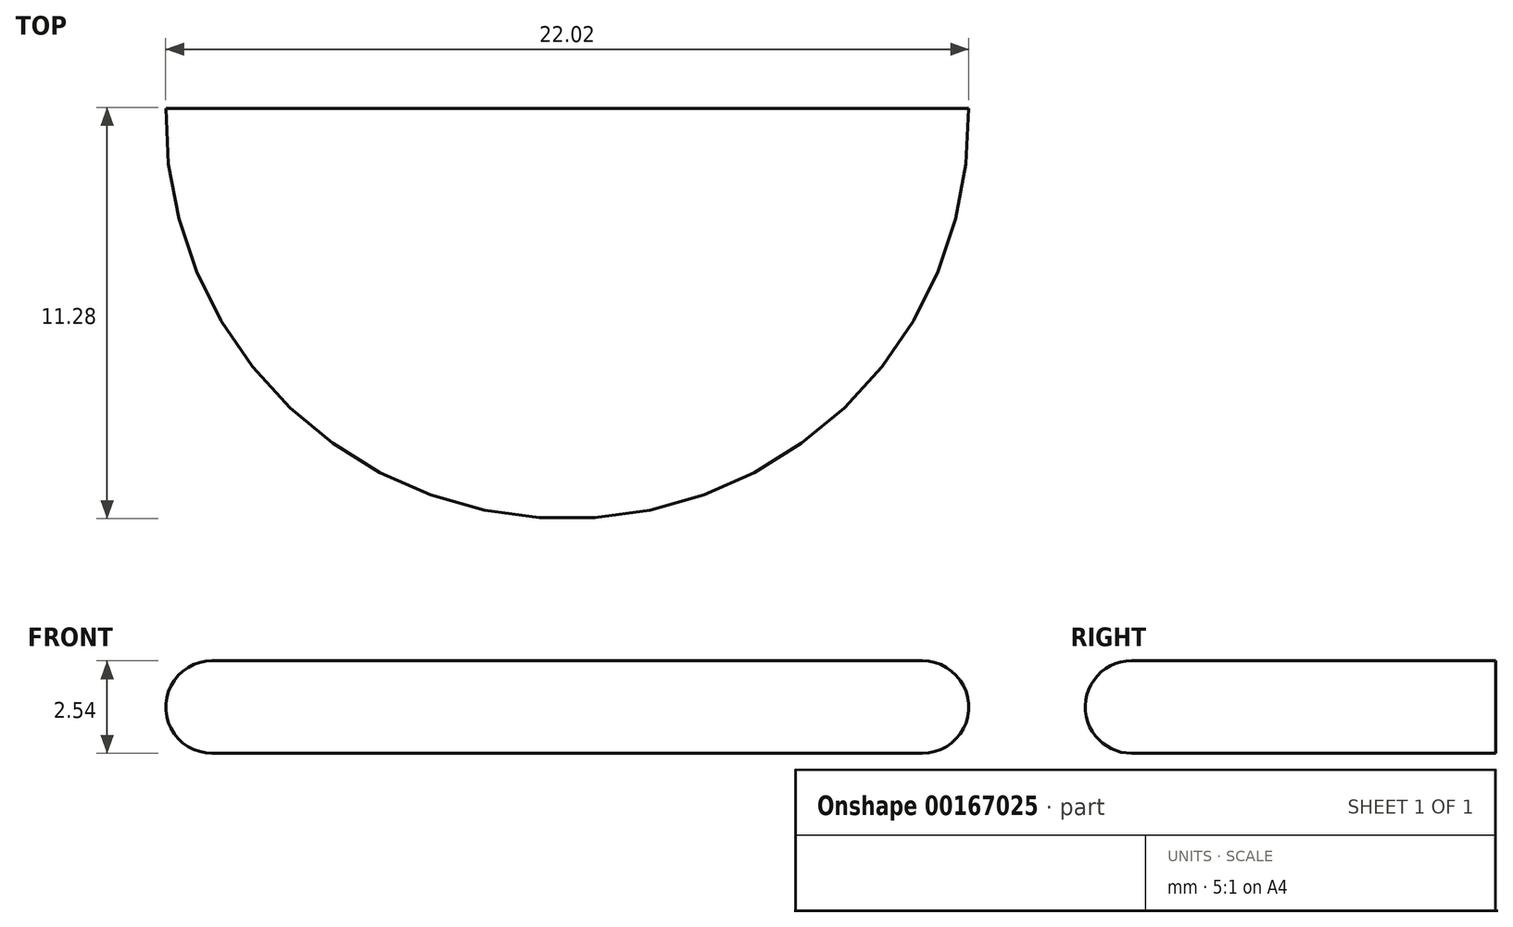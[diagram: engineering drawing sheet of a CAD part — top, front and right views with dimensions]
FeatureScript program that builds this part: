
annotation { "Feature Type Name" : "Feature", "Feature Type Description" : "" }
export const myFeature = defineFeature(function(context is Context, id is Id, definition is map)
    precondition{}
    {
        {
            var Q0;
            Q0=qCreatedBy(makeId("Top.planeOp"),FACE);
            var sketch = newSketch(context, id + "F0", { "sketchPlane" : qUnion([Q0])});
            skArc(sketch, "E0", {"start": v(-22.01, 0) * mm, "mid": v(-11, -11.25) * mm, "end": v(0, 0) * mm});
            skLineSegment(sketch, "E1", {"start": v(-22.01, 0) * mm, "end": v(0, 0) * mm});
            skSolve(sketch);
        }
        {
            var Q0;
            Q0=makeQuery(id+"F0.imprint","IMPRINT",FACE,{"disambiguationData":[TD([[makeQuery(id+"F0.imprint","IMPRINT",EDGE,{"derivedFrom":sQuery(id+"F0.wireOp",EDGE,"E0")}),1.0]])]});
            extrude(context, id + "F1", {"entities" : qUnion([Q0]), "depth" : 2.54 * mm});
        }
        {
            var Q0;
            Q0=makeQuery(id+"F1.opExtrude","CAP_EDGE",EDGE,{"disambiguationData":[OSD([sQuery(id+"F0.wireOp",EDGE,"E0")])],"isStart":false});
            var Q1;
            Q1=makeQuery(id+"F1.opExtrude","CAP_EDGE",EDGE,{"disambiguationData":[OSD([sQuery(id+"F0.wireOp",EDGE,"E0")])],"isStart":true});
            fillet(context, id + "F2", {"entities" : qUnion([Q0, Q1]), "radius" : 1.27 * mm, "tangentPropagation" : true, "allowEdgeOverflow" : false});
        }
    });
